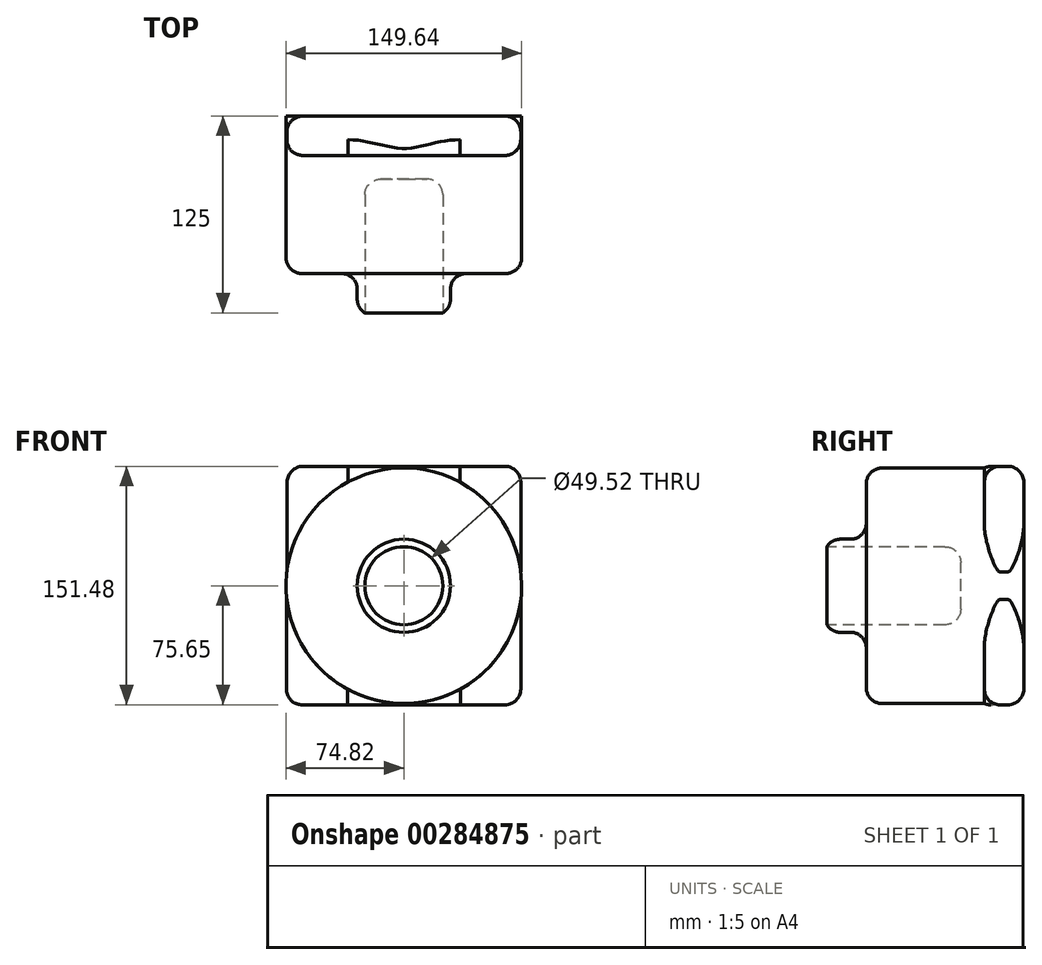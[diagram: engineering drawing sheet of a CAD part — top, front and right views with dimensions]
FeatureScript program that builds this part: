
annotation { "Feature Type Name" : "Feature", "Feature Type Description" : "" }
export const myFeature = defineFeature(function(context is Context, id is Id, definition is map)
    precondition{}
    {
        {
            var Q0;
            Q0=qCreatedBy(makeId("Front.planeOp"),FACE);
            var sketch = newSketch(context, id + "F0", { "sketchPlane" : qUnion([Q0])});
            skCircle(sketch, "E0", {"center": v(0, 0) * mm, "radius": 74.82 * mm});
            skSolve(sketch);
        }
        {
            var Q0;
            Q0=makeQuery(id+"F0.imprint","IMPRINT",FACE,{"disambiguationData":[TD([[makeQuery(id+"F0.imprint","IMPRINT",EDGE,{"derivedFrom":sQuery(id+"F0.wireOp",EDGE,"E0")}),1.0]])]});
            extrude(context, id + "F1", {"entities" : qUnion([Q0]), "depth" : 100 * mm});
        }
        {
            var Q0;
            Q0=qCreatedBy(makeId("Front.planeOp"),FACE);
            var sketch = newSketch(context, id + "F2", { "sketchPlane" : qUnion([Q0])});
            skLineSegment(sketch, "E1", {"start": v(-74.05, 75.83) * mm, "end": v(74.3, 75.83) * mm});
            skLineSegment(sketch, "E2", {"start": v(74.3, 75.83) * mm, "end": v(74.3, -75.65) * mm});
            skLineSegment(sketch, "E3", {"start": v(74.3, -75.65) * mm, "end": v(-74.6, -75.65) * mm});
            skLineSegment(sketch, "E4", {"start": v(-74.6, -75.65) * mm, "end": v(-74.05, 75.83) * mm});
            skSolve(sketch);
        }
        {
            var Q0;
            Q0=makeQuery(id+"F2.imprint","IMPRINT",FACE,{"disambiguationData":[TD([[makeQuery(id+"F2.imprint","IMPRINT",EDGE,{"derivedFrom":sQuery(id+"F2.wireOp",EDGE,"E1")}),-1.0]])]});
            extrude(context, id + "F3", {"entities" : qUnion([Q0]), "operationType" : NewBodyOperationType.ADD, "depth" : 25 * mm});
        }
        {
            var Q0;
            Q0=makeQuery(id+"F1.opExtrude","CAP_FACE",FACE,{"disambiguationData":[OSD([sQuery(id+"F0.wireOp",EDGE,"E0")])],"isStart":false});
            var sketch = newSketch(context, id + "F4", { "sketchPlane" : qUnion([Q0])});
            skCircle(sketch, "E5", {"center": v(0, 0) * mm, "radius": 29.59 * mm});
            skSolve(sketch);
        }
        {
            var Q0;
            Q0=makeQuery(id+"F4.imprint","IMPRINT",FACE,{"disambiguationData":[TD([[makeQuery(id+"F4.imprint","IMPRINT",EDGE,{"derivedFrom":sQuery(id+"F4.wireOp",EDGE,"E5")}),1.0]])]});
            extrude(context, id + "F5", {"entities" : qUnion([Q0]), "operationType" : NewBodyOperationType.ADD, "depth" : 25 * mm});
        }
        {
            var Q0;
            Q0=makeQuery(id+"F5.opExtrude","CAP_FACE",FACE,{"disambiguationData":[OSD([sQuery(id+"F4.wireOp",EDGE,"E5")])],"isStart":false});
            var sketch = newSketch(context, id + "F6", { "sketchPlane" : qUnion([Q0])});
            skCircle(sketch, "E6", {"center": v(0, 0) * mm, "radius": 24.76 * mm});
            skSolve(sketch);
        }
        {
            var Q0;
            Q0=makeQuery(id+"F6.imprint","IMPRINT",FACE,{"disambiguationData":[TD([[makeQuery(id+"F6.imprint","IMPRINT",EDGE,{"derivedFrom":sQuery(id+"F6.wireOp",EDGE,"E6")}),1.0]])]});
            extrude(context, id + "F7", {"entities" : qUnion([Q0]), "operationType" : NewBodyOperationType.REMOVE, "oppositeDirection" : true, "depth" : 85 * mm});
        }
        {
            var Q0;
            Q0=makeQuery(id+"F3.opExtrude","CAP_EDGE",EDGE,{"disambiguationData":[OSD([sQuery(id+"F2.wireOp",EDGE,"E1")])],"isStart":false});
            var Q1;
            {var subQ0=sQuery(id+"F2.wireOp",EDGE,"E2");var subQ1=sQuery(id+"F2.wireOp",EDGE,"E1");Q1=makeQuery(id+"F3.boolean.opBoolean","SPLIT",EDGE,{"disambiguationData":[TD([makeQuery(id+"F3.opExtrude","SWEPT_FACE",FACE,{"disambiguationData":[OSD([subQ1])]})])],"derivedFrom":makeQuery(id+"F3.opExtrude","CAP_EDGE",EDGE,{"disambiguationData":[OSD([subQ0])],"isStart":false})});}
            var Q2;
            {var subQ0=sQuery(id+"F2.wireOp",EDGE,"E4");var subQ1=sQuery(id+"F2.wireOp",EDGE,"E1");Q2=makeQuery(id+"F3.boolean.opBoolean","SPLIT",EDGE,{"disambiguationData":[TD([makeQuery(id+"F3.opExtrude","SWEPT_FACE",FACE,{"disambiguationData":[OSD([subQ1])]})])],"derivedFrom":makeQuery(id+"F3.opExtrude","CAP_EDGE",EDGE,{"disambiguationData":[OSD([subQ0])],"isStart":false})});}
            var Q3;
            Q3=makeQuery(id+"F3.opExtrude","SWEPT_EDGE",EDGE,{"disambiguationData":[OSD([sQuery(id+"F2.wireOp",EDGE,"E1"),sQuery(id+"F2.wireOp",EDGE,"E2")])]});
            var Q4;
            Q4=makeQuery(id+"F3.opExtrude","SWEPT_EDGE",EDGE,{"disambiguationData":[OSD([sQuery(id+"F2.wireOp",EDGE,"E1"),sQuery(id+"F2.wireOp",EDGE,"E4")])]});
            var Q5;
            Q5=makeQuery(id+"F3.opExtrude","CAP_EDGE",EDGE,{"disambiguationData":[OSD([sQuery(id+"F2.wireOp",EDGE,"E1")])],"isStart":true});
            var Q6;
            {var subQ0=sQuery(id+"F2.wireOp",EDGE,"E4");var subQ1=sQuery(id+"F2.wireOp",EDGE,"E1");Q6=makeQuery(id+"F3.boolean.opBoolean","SPLIT",EDGE,{"disambiguationData":[TD([makeQuery(id+"F3.opExtrude","SWEPT_FACE",FACE,{"disambiguationData":[OSD([subQ1])]})])],"derivedFrom":makeQuery(id+"F3.opExtrude","CAP_EDGE",EDGE,{"disambiguationData":[OSD([subQ0])],"isStart":true})});}
            var Q7;
            {var subQ0=sQuery(id+"F2.wireOp",EDGE,"E2");var subQ1=sQuery(id+"F2.wireOp",EDGE,"E1");Q7=makeQuery(id+"F3.boolean.opBoolean","SPLIT",EDGE,{"disambiguationData":[TD([makeQuery(id+"F3.opExtrude","SWEPT_FACE",FACE,{"disambiguationData":[OSD([subQ1])]})])],"derivedFrom":makeQuery(id+"F3.opExtrude","CAP_EDGE",EDGE,{"disambiguationData":[OSD([subQ0])],"isStart":true})});}
            var Q8;
            {var subQ0=sQuery(id+"F2.wireOp",EDGE,"E4");var subQ1=sQuery(id+"F2.wireOp",EDGE,"E3");Q8=makeQuery(id+"F3.boolean.opBoolean","SPLIT",EDGE,{"disambiguationData":[TD([makeQuery(id+"F3.opExtrude","SWEPT_FACE",FACE,{"disambiguationData":[OSD([subQ1])]})])],"derivedFrom":makeQuery(id+"F3.opExtrude","CAP_EDGE",EDGE,{"disambiguationData":[OSD([subQ0])],"isStart":false})});}
            var Q9;
            {var subQ0=sQuery(id+"F2.wireOp",EDGE,"E3");var subQ1=sQuery(id+"F2.wireOp",EDGE,"E4");Q9=makeQuery(id+"F3.boolean.opBoolean","SPLIT",EDGE,{"disambiguationData":[TD([makeQuery(id+"F3.opExtrude","SWEPT_FACE",FACE,{"disambiguationData":[OSD([subQ0])]})])],"derivedFrom":makeQuery(id+"F3.opExtrude","CAP_EDGE",EDGE,{"disambiguationData":[OSD([subQ1])],"isStart":true})});}
            var Q10;
            Q10=makeQuery(id+"F3.opExtrude","CAP_EDGE",EDGE,{"disambiguationData":[OSD([sQuery(id+"F2.wireOp",EDGE,"E3")])],"isStart":false});
            var Q11;
            Q11=makeQuery(id+"F3.opExtrude","CAP_EDGE",EDGE,{"disambiguationData":[OSD([sQuery(id+"F2.wireOp",EDGE,"E3")])],"isStart":true});
            var Q12;
            {var subQ0=sQuery(id+"F2.wireOp",EDGE,"E3");var subQ1=sQuery(id+"F2.wireOp",EDGE,"E2");Q12=makeQuery(id+"F3.boolean.opBoolean","SPLIT",EDGE,{"disambiguationData":[TD([makeQuery(id+"F3.opExtrude","SWEPT_FACE",FACE,{"disambiguationData":[OSD([subQ0])]})])],"derivedFrom":makeQuery(id+"F3.opExtrude","CAP_EDGE",EDGE,{"disambiguationData":[OSD([subQ1])],"isStart":true})});}
            var Q13;
            Q13=makeQuery(id+"F3.opExtrude","SWEPT_EDGE",EDGE,{"disambiguationData":[OSD([sQuery(id+"F2.wireOp",EDGE,"E2"),sQuery(id+"F2.wireOp",EDGE,"E3")])]});
            var Q14;
            {var subQ0=sQuery(id+"F2.wireOp",EDGE,"E3");var subQ1=sQuery(id+"F2.wireOp",EDGE,"E2");Q14=makeQuery(id+"F3.boolean.opBoolean","SPLIT",EDGE,{"disambiguationData":[TD([makeQuery(id+"F3.opExtrude","SWEPT_FACE",FACE,{"disambiguationData":[OSD([subQ0])]})])],"derivedFrom":makeQuery(id+"F3.opExtrude","CAP_EDGE",EDGE,{"disambiguationData":[OSD([subQ1])],"isStart":false})});}
            var Q15;
            Q15=makeQuery(id+"F1.opExtrude","CAP_EDGE",EDGE,{"disambiguationData":[OSD([sQuery(id+"F0.wireOp",EDGE,"E0")])],"isStart":false});
            var Q16;
            Q16=makeQuery(id+"F5.opExtrude","CAP_EDGE",EDGE,{"disambiguationData":[OSD([sQuery(id+"F4.wireOp",EDGE,"E5")])],"isStart":true});
            var Q17;
            Q17=makeQuery(id+"F7.boolean.opBoolean","COPY",EDGE,{"derivedFrom":makeQuery(id+"F7.opExtrude","CAP_EDGE",EDGE,{"disambiguationData":[OSD([sQuery(id+"F6.wireOp",EDGE,"E6")])],"isStart":false})});
            var Q18;
            Q18=makeQuery(id+"F5.opExtrude","SWEPT_FACE",FACE,{"disambiguationData":[OSD([sQuery(id+"F4.wireOp",EDGE,"E5")])]});
            var Q19;
            Q19=makeQuery(id+"F5.opExtrude","CAP_EDGE",EDGE,{"disambiguationData":[OSD([sQuery(id+"F4.wireOp",EDGE,"E5")])],"isStart":false});
            var Q20;
            Q20=makeQuery(id+"F3.opExtrude","SWEPT_EDGE",EDGE,{"disambiguationData":[OSD([sQuery(id+"F2.wireOp",EDGE,"E3"),sQuery(id+"F2.wireOp",EDGE,"E4")])]});
            fillet(context, id + "F8", {"entities" : qUnion([Q0, Q1, Q2, Q3, Q4, Q5, Q6, Q7, Q8, Q9, Q10, Q11, Q12, Q13, Q14, Q15, Q16, Q17, Q18, Q19, Q20]), "radius" : 10 * mm, "tangentPropagation" : true, "allowEdgeOverflow" : false});
        }
    });
